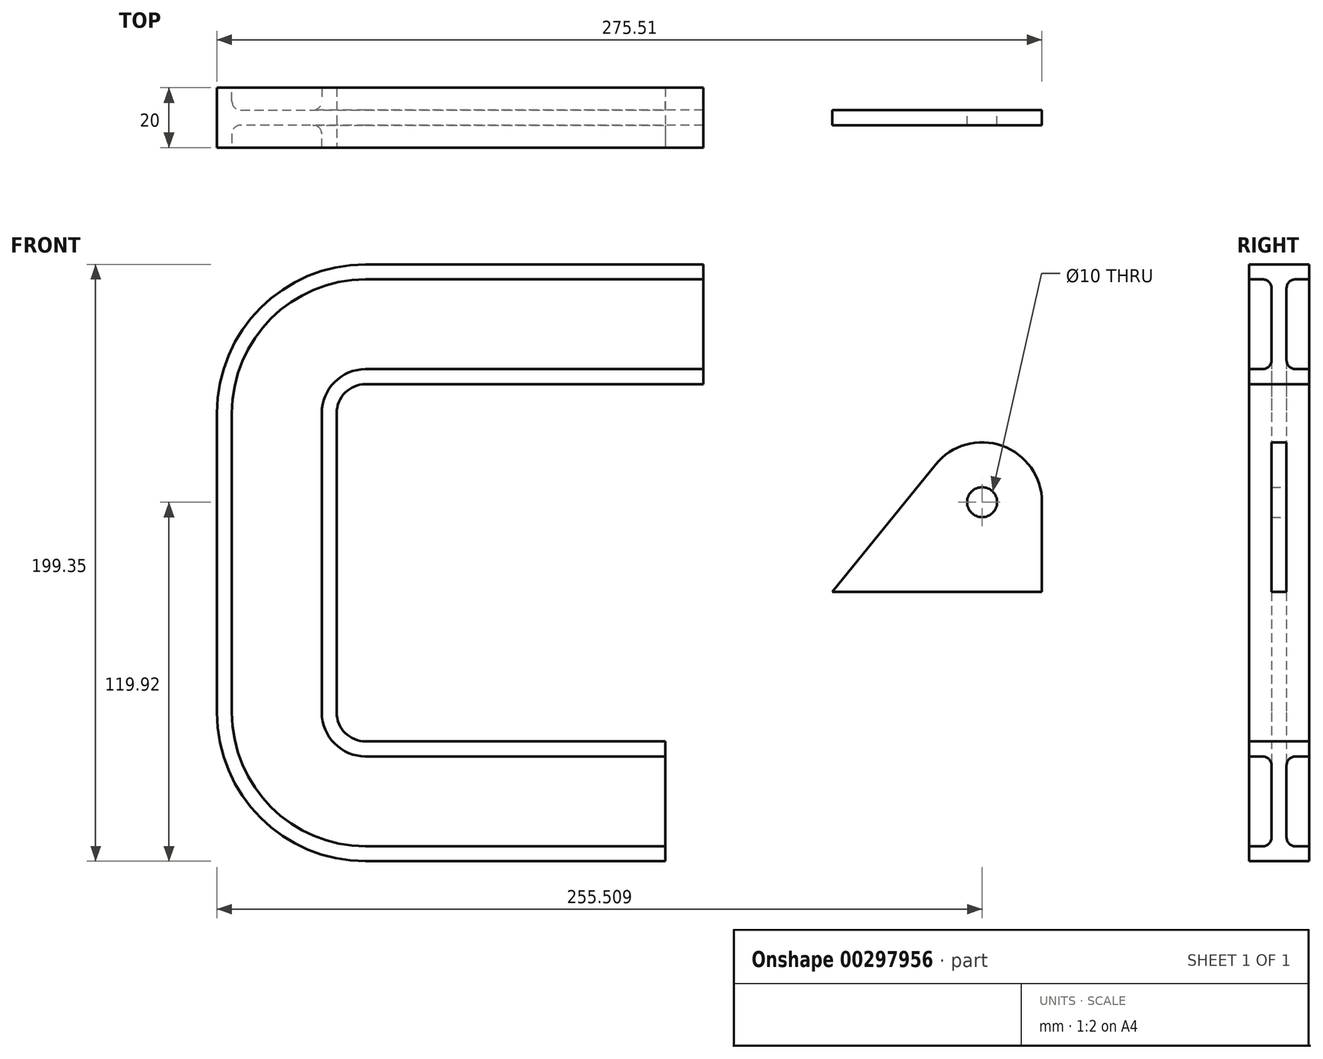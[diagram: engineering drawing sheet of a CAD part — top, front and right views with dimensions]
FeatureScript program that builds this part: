
annotation { "Feature Type Name" : "Feature", "Feature Type Description" : "" }
export const myFeature = defineFeature(function(context is Context, id is Id, definition is map)
    precondition{}
    {
        {
            var Q0;
            Q0=qCreatedBy(makeId("Right.planeOp"),FACE);
            var sketch = newSketch(context, id + "F0", { "sketchPlane" : qUnion([Q0])});
            skLineSegment(sketch, "E0", {"start": v(0, 69.43) * mm, "end": v(10, 69.43) * mm});
            skLineSegment(sketch, "E1", {"start": v(10, 69.43) * mm, "end": v(10, 74.43) * mm});
            skLineSegment(sketch, "E2", {"start": v(10, 74.43) * mm, "end": v(5.5, 74.43) * mm});
            skLineSegment(sketch, "E3", {"start": v(2.5, 77.43) * mm, "end": v(2.5, 101.43) * mm});
            skLineSegment(sketch, "E4", {"start": v(5.5, 104.43) * mm, "end": v(10, 104.43) * mm});
            skLineSegment(sketch, "E5", {"start": v(10, 109.43) * mm, "end": v(10, 104.43) * mm});
            skLineSegment(sketch, "E6", {"start": v(10, 109.43) * mm, "end": v(0, 109.43) * mm});
            skLineSegment(sketch, "E7.MirrorCS", {"start": v(-10, 74.43) * mm, "end": v(-5.5, 74.43) * mm});
            skLineSegment(sketch, "E8.MirrorCS", {"start": v(-10, 109.43) * mm, "end": v(-10, 104.43) * mm});
            skLineSegment(sketch, "E9.MirrorCS", {"start": v(-5.5, 104.43) * mm, "end": v(-10, 104.43) * mm});
            skLineSegment(sketch, "E10.MirrorCS", {"start": v(-10, 69.43) * mm, "end": v(-10, 74.43) * mm});
            skLineSegment(sketch, "E11.MirrorCS", {"start": v(-10, 109.43) * mm, "end": v(0, 109.43) * mm});
            skLineSegment(sketch, "E12.MirrorCS", {"start": v(-2.5, 77.43) * mm, "end": v(-2.5, 101.43) * mm});
            skLineSegment(sketch, "E13.MirrorCS", {"start": v(0, 69.43) * mm, "end": v(-10, 69.43) * mm});
            skArc(sketch, "E14", {"start": v(-5.5, 74.43) * mm, "mid": v(-3.38, 75.3) * mm, "end": v(-2.5, 77.43) * mm});
            skArc(sketch, "E15", {"start": v(2.5, 77.43) * mm, "mid": v(3.38, 75.3) * mm, "end": v(5.5, 74.43) * mm});
            skArc(sketch, "E16", {"start": v(-5.5, 104.43) * mm, "mid": v(-3.38, 103.55) * mm, "end": v(-2.5, 101.43) * mm});
            skArc(sketch, "E17", {"start": v(2.5, 101.43) * mm, "mid": v(3.38, 103.55) * mm, "end": v(5.5, 104.43) * mm});
            skSolve(sketch);
        }
        {
            var Q0;
            Q0=qCreatedBy(makeId("Front.planeOp"),FACE);
            var sketch = newSketch(context, id + "F1", { "sketchPlane" : qUnion([Q0])});
            skLineSegment(sketch, "E18", {"start": v(0, 69.75) * mm, "end": v(-100, 69.75) * mm});
            skArc(sketch, "E19", {"start": v(-100, 69.75) * mm, "mid": v(-107.07, 66.82) * mm, "end": v(-110, 59.75) * mm});
            skLineSegment(sketch, "E20", {"start": v(-110, 59.75) * mm, "end": v(-110, -40.25) * mm});
            skArc(sketch, "E21", {"start": v(-110, -40.25) * mm, "mid": v(-107.07, -47.32) * mm, "end": v(-100, -50.25) * mm});
            skLineSegment(sketch, "E22", {"start": v(-100, -50.25) * mm, "end": v(0, -50.25) * mm});
            skSolve(sketch);
        }
        {
            var Q0;
            Q0 = qSketchRegion(id + "F0", true);
            extrude(context, id + "F2", {"entities" : qUnion([Q0]), "endBound" : BoundingType.SYMMETRIC, "depth" : 25.4 * mm});
        }
        {
            var Q0;
            Q0 = qSketchRegion(id + "F0", true);
            var Q1;
            Q1 = qConstructionFilter(qBodyType(qCreatedBy(id + "F1" ,EDGE), BodyType.WIRE), ConstructionObject.NO);
            sweep(context, id + "F3", {"operationType" : NewBodyOperationType.ADD, "profiles" : qUnion([Q0]), "path" : qUnion([Q1])});
        }
        {
            var Q0;
            Q0=qCreatedBy(makeId("Front.planeOp"),FACE);
            var sketch = newSketch(context, id + "F4", { "sketchPlane" : qUnion([Q0])});
            skLineSegment(sketch, "E23", {"start": v(55.84, 0) * mm, "end": v(125.84, 0) * mm});
            skLineSegment(sketch, "E24", {"start": v(125.84, 0) * mm, "end": v(125.84, 30) * mm});
            skArc(sketch, "E25", {"start": v(125.84, 30) * mm, "mid": v(112.51, 48.85) * mm, "end": v(90.3, 42.58) * mm});
            skLineSegment(sketch, "E26", {"start": v(55.84, 0) * mm, "end": v(90.3, 42.58) * mm});
            skCircle(sketch, "E27", {"center": v(105.84, 30) * mm, "radius": 5 * mm});
            skSolve(sketch);
        }
        {
            var Q0;
            Q0 = qSketchRegion(id + "F4", true);
            extrude(context, id + "F5", {"entities" : qUnion([Q0]), "endBound" : BoundingType.SYMMETRIC, "depth" : 5 * mm});
        }
    });
